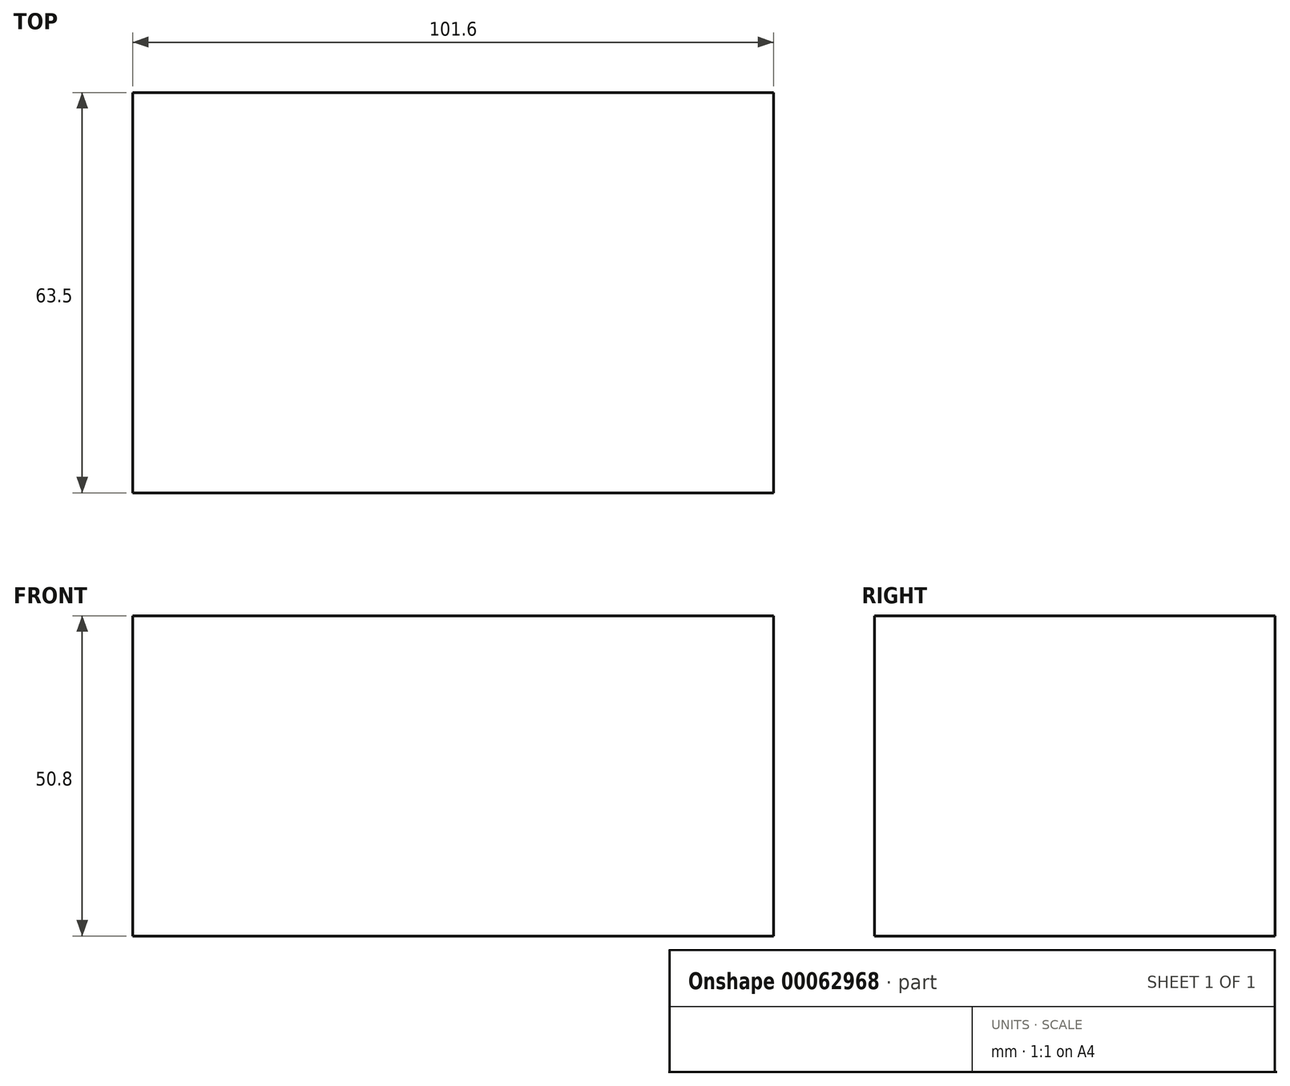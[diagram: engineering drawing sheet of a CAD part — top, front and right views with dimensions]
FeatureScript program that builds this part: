
annotation { "Feature Type Name" : "Feature", "Feature Type Description" : "" }
export const myFeature = defineFeature(function(context is Context, id is Id, definition is map)
    precondition{}
    {
        {
            var Q0;
            Q0=qCreatedBy(makeId("Front.planeOp"),FACE);
            var sketch = newSketch(context, id + "F0", { "sketchPlane" : qUnion([Q0])});
            skLineSegment(sketch, "E0.bottom", {"start": v(101.6, 0) * mm, "end": v(0, 0) * mm});
            skLineSegment(sketch, "E0.top", {"start": v(101.6, 50.8) * mm, "end": v(0, 50.8) * mm});
            skLineSegment(sketch, "E0.left", {"start": v(101.6, 0) * mm, "end": v(101.6, 50.8) * mm});
            skLineSegment(sketch, "E0.right", {"start": v(0, 0) * mm, "end": v(0, 50.8) * mm});
            skSolve(sketch);
        }
        {
            var Q0;
            Q0=makeQuery(id+"F0.imprint","IMPRINT",FACE,{"disambiguationData":[TD([[makeQuery(id+"F0.imprint","IMPRINT",EDGE,{"derivedFrom":sQuery(id+"F0.wireOp",EDGE,"E0.bottom")}),-1.0]])]});
            extrude(context, id + "F1", {"entities" : qUnion([Q0]), "depth" : 63.5 * mm});
        }
    });
